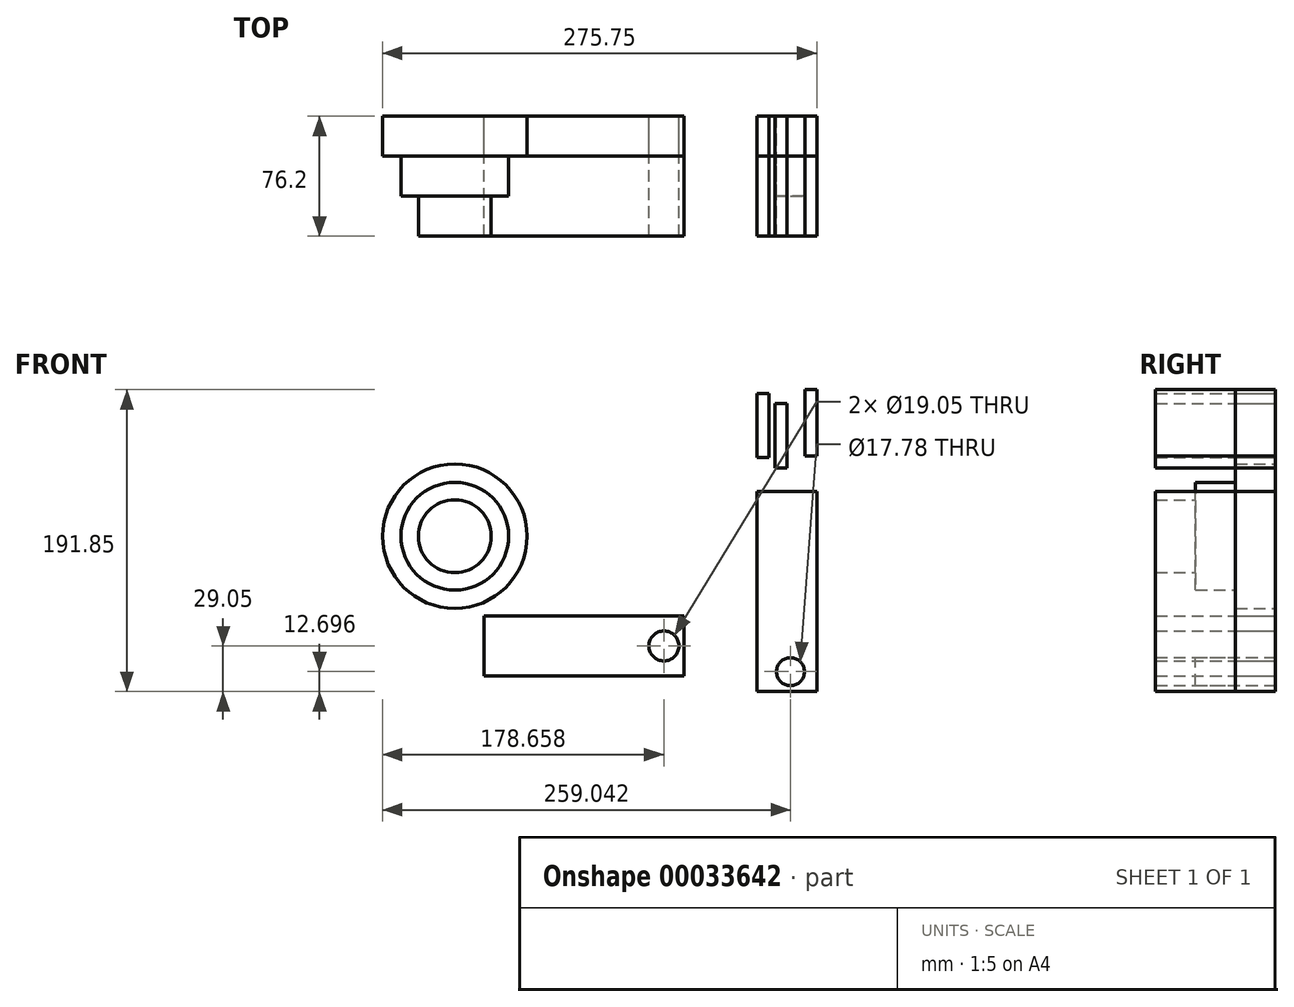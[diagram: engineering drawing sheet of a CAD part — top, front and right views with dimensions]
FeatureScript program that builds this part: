
annotation { "Feature Type Name" : "Feature", "Feature Type Description" : "" }
export const myFeature = defineFeature(function(context is Context, id is Id, definition is map)
    precondition{}
    {
        {
            var Q0;
            Q0=qCreatedBy(makeId("Front.planeOp"),FACE);
            var sketch = newSketch(context, id + "F0", { "sketchPlane" : qUnion([Q0])});
            skLineSegment(sketch, "E0.bottom", {"start": v(-67.41, 0) * mm, "end": v(59.59, 0) * mm});
            skLineSegment(sketch, "E0.top", {"start": v(-67.41, -38.1) * mm, "end": v(59.59, -38.1) * mm});
            skLineSegment(sketch, "E0.left", {"start": v(-67.41, 0) * mm, "end": v(-67.41, -38.1) * mm});
            skLineSegment(sketch, "E0.right", {"start": v(59.59, 0) * mm, "end": v(59.59, -38.1) * mm});
            skLineSegment(sketch, "E1.bottom", {"start": v(59.59, -38.1) * mm, "end": v(40.54, -38.1) * mm});
            skLineSegment(sketch, "E2.bottom", {"start": v(105.88, 78.9) * mm, "end": v(143.98, 78.9) * mm});
            skLineSegment(sketch, "E2.top", {"start": v(105.88, -48.1) * mm, "end": v(143.98, -48.1) * mm});
            skLineSegment(sketch, "E2.left", {"start": v(105.88, 78.9) * mm, "end": v(105.88, -48.1) * mm});
            skLineSegment(sketch, "E2.right", {"start": v(143.98, 78.9) * mm, "end": v(143.98, -48.1) * mm});
            skLineSegment(sketch, "E3.bottom", {"start": v(105.88, 100.7) * mm, "end": v(113.5, 100.7) * mm});
            skLineSegment(sketch, "E3.top", {"start": v(105.88, 141.19) * mm, "end": v(113.5, 141.19) * mm});
            skLineSegment(sketch, "E3.left", {"start": v(105.88, 100.7) * mm, "end": v(105.88, 141.19) * mm});
            skLineSegment(sketch, "E3.right", {"start": v(113.5, 100.7) * mm, "end": v(113.5, 141.19) * mm});
            skLineSegment(sketch, "E4.bottom", {"start": v(143.98, 101.73) * mm, "end": v(136.36, 101.73) * mm});
            skLineSegment(sketch, "E4.top", {"start": v(143.98, 143.75) * mm, "end": v(136.36, 143.75) * mm});
            skLineSegment(sketch, "E4.left", {"start": v(143.98, 101.73) * mm, "end": v(143.98, 143.75) * mm});
            skLineSegment(sketch, "E4.right", {"start": v(136.36, 101.73) * mm, "end": v(136.36, 143.75) * mm});
            skPoint(sketch, "E5.firstSnap0", {"position": v(124.93, 78.9) * mm});
            skLineSegment(sketch, "E5.bottom", {"start": v(124.93, 94.1) * mm, "end": v(117.31, 94.1) * mm});
            skLineSegment(sketch, "E5.top", {"start": v(124.93, 134.97) * mm, "end": v(117.31, 134.97) * mm});
            skLineSegment(sketch, "E5.left", {"start": v(124.93, 94.1) * mm, "end": v(124.93, 134.97) * mm});
            skLineSegment(sketch, "E5.right", {"start": v(117.31, 94.1) * mm, "end": v(117.31, 134.97) * mm});
            skCircle(sketch, "E6", {"center": v(46.89, -19.05) * mm, "radius": 9.53 * mm});
            skCircle(sketch, "E7", {"center": v(127.27, -35.4) * mm, "radius": 8.9 * mm});
            skCircle(sketch, "E8", {"center": v(-85.9, 50.65) * mm, "radius": 45.87 * mm});
            skCircle(sketch, "E9", {"center": v(-85.9, 50.65) * mm, "radius": 34.19 * mm});
            skCircle(sketch, "E10", {"center": v(-85.9, 50.65) * mm, "radius": 23.16 * mm});
            skSolve(sketch);
        }
        {
            var Q0;
            Q0=makeQuery(id+"F0.imprint","IMPRINT",FACE,{"disambiguationData":[TD([[makeQuery(id+"F0.imprint","IMPRINT",EDGE,{"derivedFrom":sQuery(id+"F0.wireOp",EDGE,"E0.bottom")}),-1.0]])]});
            extrude(context, id + "F1", {"entities" : qUnion([Q0]), "depth" : 25.4 * mm});
        }
        {
            var Q0;
            Q0=makeQuery(id+"F0.imprint","IMPRINT",FACE,{"disambiguationData":[TD([[makeQuery(id+"F0.imprint","IMPRINT",EDGE,{"derivedFrom":sQuery(id+"F0.wireOp",EDGE,"E2.bottom")}),-1.0]])]});
            extrude(context, id + "F2", {"entities" : qUnion([Q0]), "depth" : 25.4 * mm});
        }
        {
            var Q0;
            Q0=makeQuery(id+"F0.imprint","IMPRINT",FACE,{"disambiguationData":[TD([[makeQuery(id+"F0.imprint","IMPRINT",EDGE,{"derivedFrom":sQuery(id+"F0.wireOp",EDGE,"E7")}),1.0]])]});
            extrude(context, id + "F3", {"entities" : qUnion([Q0]), "operationType" : NewBodyOperationType.ADD, "depth" : 50.8 * mm});
        }
        {
            var Q0;
            Q0=makeQuery(id+"F0.imprint","IMPRINT",FACE,{"disambiguationData":[TD([[makeQuery(id+"F0.imprint","IMPRINT",EDGE,{"derivedFrom":sQuery(id+"F0.wireOp",EDGE,"E3.bottom")}),1.0]])]});
            var Q1;
            Q1=makeQuery(id+"F0.imprint","IMPRINT",FACE,{"disambiguationData":[TD([[makeQuery(id+"F0.imprint","IMPRINT",EDGE,{"derivedFrom":sQuery(id+"F0.wireOp",EDGE,"E5.bottom")}),-1.0]])]});
            var Q2;
            Q2=makeQuery(id+"F0.imprint","IMPRINT",FACE,{"disambiguationData":[TD([[makeQuery(id+"F0.imprint","IMPRINT",EDGE,{"derivedFrom":sQuery(id+"F0.wireOp",EDGE,"E4.bottom")}),-1.0]])]});
            extrude(context, id + "F4", {"entities" : qUnion([Q0, Q1, Q2]), "depth" : 25.4 * mm});
        }
        {
            var Q0;
            Q0=makeQuery(id+"F0.imprint","IMPRINT",FACE,{"disambiguationData":[TD([[makeQuery(id+"F0.imprint","IMPRINT",EDGE,{"derivedFrom":sQuery(id+"F0.wireOp",EDGE,"E3.bottom")}),1.0]])]});
            var Q1;
            Q1=makeQuery(id+"F0.imprint","IMPRINT",FACE,{"disambiguationData":[TD([[makeQuery(id+"F0.imprint","IMPRINT",EDGE,{"derivedFrom":sQuery(id+"F0.wireOp",EDGE,"E4.bottom")}),-1.0]])]});
            var Q2;
            Q2=makeQuery(id+"F0.imprint","IMPRINT",FACE,{"disambiguationData":[TD([[makeQuery(id+"F0.imprint","IMPRINT",EDGE,{"derivedFrom":sQuery(id+"F0.wireOp",EDGE,"E5.bottom")}),-1.0]])]});
            var Q3;
            Q3=makeQuery(id+"F0.imprint","IMPRINT",FACE,{"disambiguationData":[TD([[makeQuery(id+"F0.imprint","IMPRINT",EDGE,{"derivedFrom":sQuery(id+"F0.wireOp",EDGE,"E0.bottom")}),-1.0]])]});
            var Q4;
            Q4=makeQuery(id+"F0.imprint","IMPRINT",FACE,{"disambiguationData":[TD([[makeQuery(id+"F0.imprint","IMPRINT",EDGE,{"derivedFrom":sQuery(id+"F0.wireOp",EDGE,"E2.bottom")}),-1.0]])]});
            var Q5;
            Q5=makeQuery(id+"F0.imprint","IMPRINT",FACE,{"disambiguationData":[TD([[makeQuery(id+"F0.imprint","IMPRINT",EDGE,{"derivedFrom":sQuery(id+"F0.wireOp",EDGE,"E10")}),1.0]])]});
            extrude(context, id + "F5", {"entities" : qUnion([Q0, Q1, Q2, Q3, Q4, Q5]), "depth" : 76.2 * mm});
        }
        {
            var Q0;
            Q0=makeQuery(id+"F0.imprint","IMPRINT",FACE,{"disambiguationData":[TD([[makeQuery(id+"F0.imprint","IMPRINT",EDGE,{"derivedFrom":sQuery(id+"F0.wireOp",EDGE,"E9")}),1.0]])]});
            extrude(context, id + "F6", {"entities" : qUnion([Q0]), "operationType" : NewBodyOperationType.ADD, "depth" : 50.8 * mm});
        }
        {
            var Q0;
            Q0=makeQuery(id+"F0.imprint","IMPRINT",FACE,{"disambiguationData":[TD([[makeQuery(id+"F0.imprint","IMPRINT",EDGE,{"derivedFrom":sQuery(id+"F0.wireOp",EDGE,"E8")}),1.0]])]});
            extrude(context, id + "F7", {"entities" : qUnion([Q0]), "operationType" : NewBodyOperationType.ADD, "depth" : 25.4 * mm});
        }
    });
